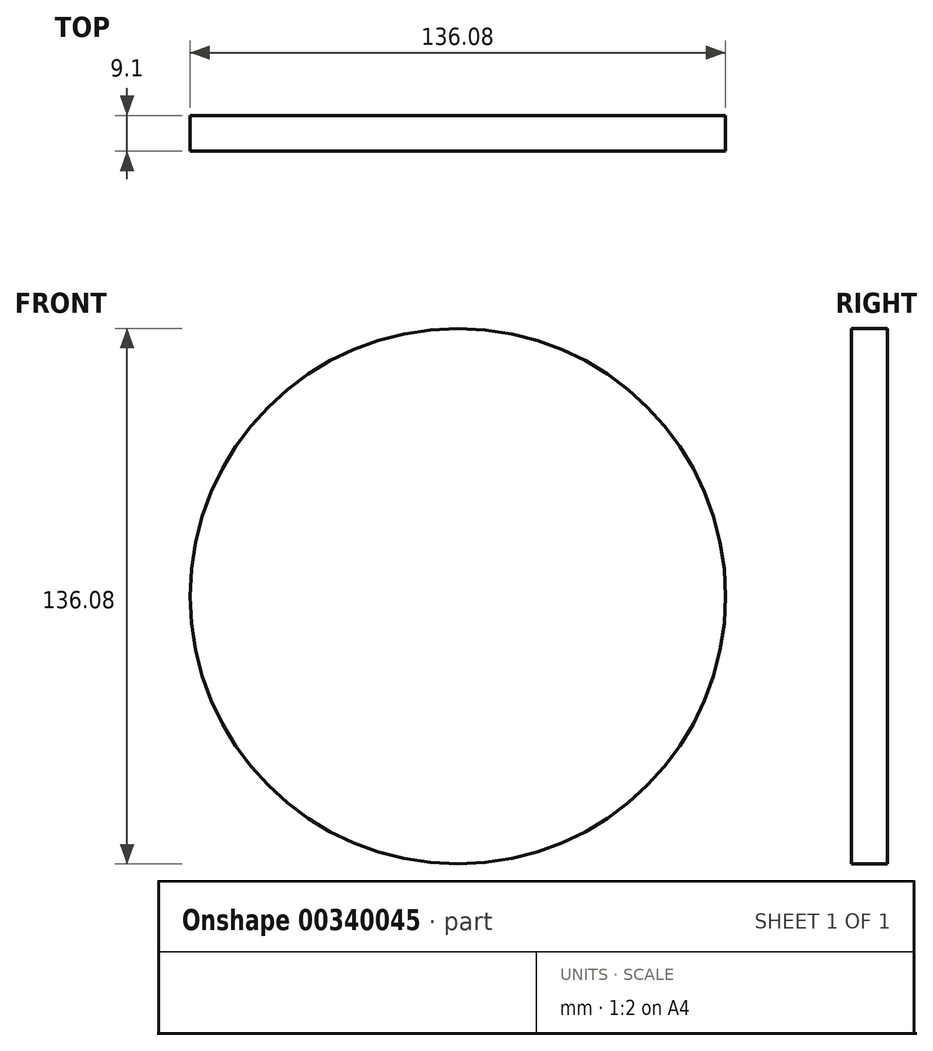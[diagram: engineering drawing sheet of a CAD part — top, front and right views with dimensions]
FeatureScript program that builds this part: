
annotation { "Feature Type Name" : "Feature", "Feature Type Description" : "" }
export const myFeature = defineFeature(function(context is Context, id is Id, definition is map)
    precondition{}
    {
        {
            var Q0;
            Q0=qCreatedBy(makeId("Front.planeOp"),FACE);
            var sketch = newSketch(context, id + "F0", { "sketchPlane" : qUnion([Q0])});
            skCircle(sketch, "E0", {"center": v(0, 0) * mm, "radius": 68.04 * mm});
            skSolve(sketch);
        }
        {
            var Q0;
            Q0 = qSketchRegion(id + "F0", true);
            extrude(context, id + "F1", {"entities" : qUnion([Q0]), "depth" : 9.1 * mm});
        }
    });
